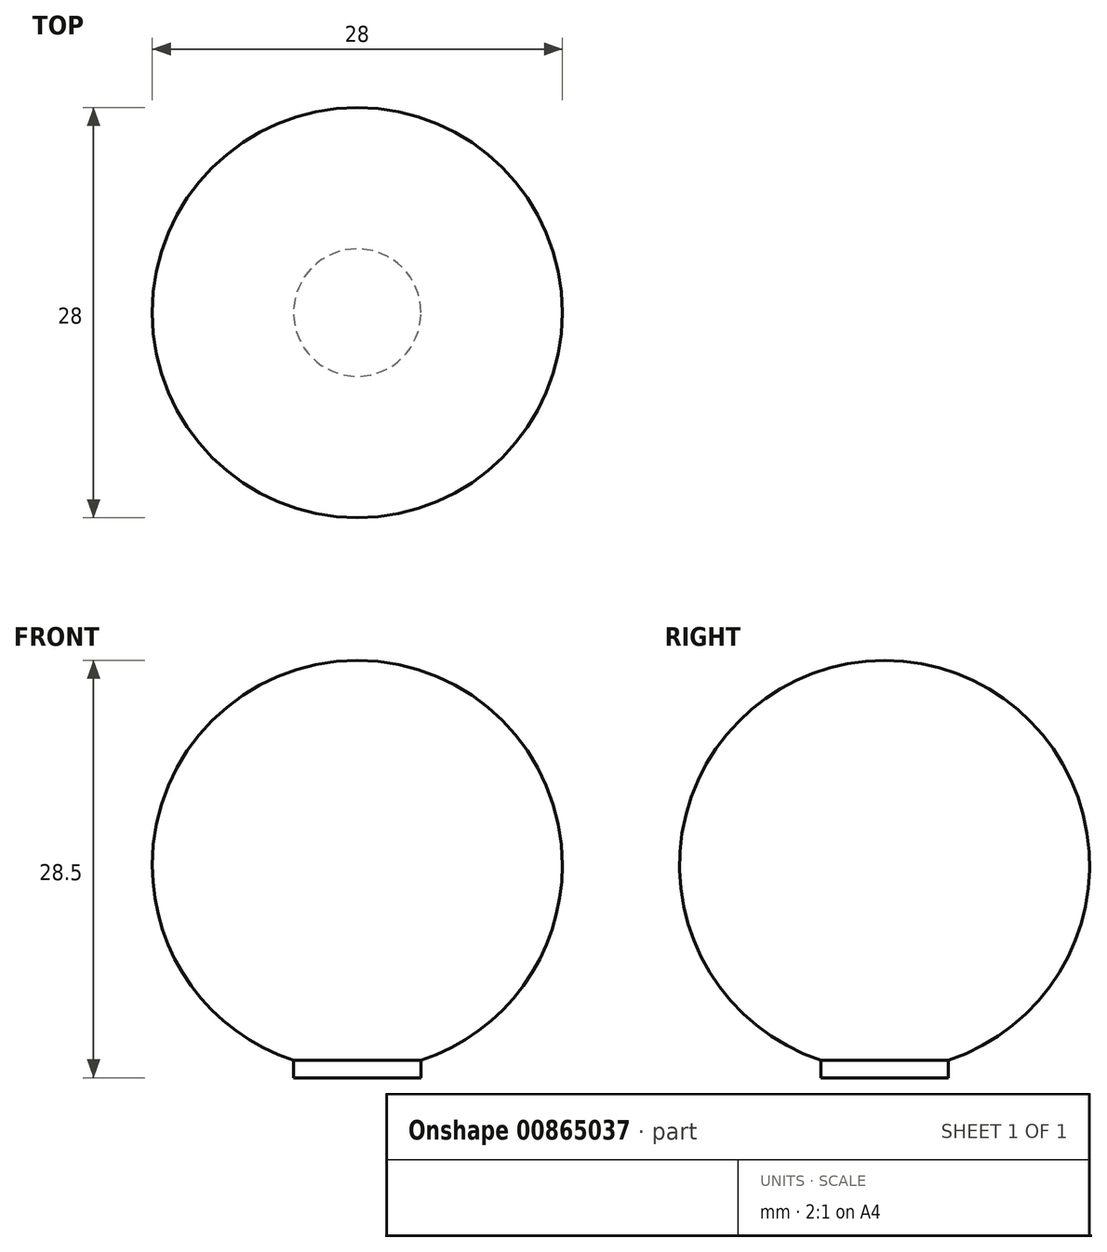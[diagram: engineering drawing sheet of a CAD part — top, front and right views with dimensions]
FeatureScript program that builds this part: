
annotation { "Feature Type Name" : "Feature", "Feature Type Description" : "" }
export const myFeature = defineFeature(function(context is Context, id is Id, definition is map)
    precondition{}
    {
        {
            var Q0;
            Q0=qCreatedBy(makeId("Front.planeOp"),FACE);
            var sketch = newSketch(context, id + "F0", { "sketchPlane" : qUnion([Q0])});
            skCircle(sketch, "E0", {"center": v(0, 0) * mm, "radius": 14 * mm});
            skLineSegment(sketch, "E1", {"start": v(-14, 0) * mm, "end": v(14, 0) * mm});
            skSolve(sketch);
        }
        {
            var Q0;
            {var subQ0=sQuery(id+"F0.wireOp",EDGE,"E1");Q0=makeQuery(id+"F0.imprint","IMPRINT",FACE,{"disambiguationData":[TD([[makeQuery(id+"F0.imprint","IMPRINT",EDGE,{"derivedFrom":subQ0}),-1.0]])]});}
            var Q1;
            Q1=sQuery(id+"F0.wireOp",EDGE,"E1");
            revolve(context, id + "F1", {"surfaceOperationType" : NewSurfaceOperationType.NEW, "entities" : qUnion([Q0]), "axis" : qUnion([Q1]), "revolveType" : RevolveType.FULL});
        }
        {
            var Q0;
            Q0=qCreatedBy(makeId("Top.planeOp"),FACE);
            cPlane(context, id + "F2", {"entities" : qUnion([Q0]), "cplaneType" : CPlaneType.OFFSET, "offset" : 12.5 * mm, "oppositeDirection" : true, "width" : 150 * mm, "height" : 150 * mm});
        }
        {
            var Q0;
            Q0=qCreatedBy(id+"F2.planeOp",FACE);
            var sketch = newSketch(context, id + "F3", { "sketchPlane" : qUnion([Q0])});
            skCircle(sketch, "E2", {"center": v(0, 0) * mm, "radius": 4.35 * mm});
            skSolve(sketch);
        }
        {
            var Q0;
            Q0 = qSketchRegion(id + "F3", true);
            extrude(context, id + "F4", {"entities" : qUnion([Q0]), "operationType" : NewBodyOperationType.ADD, "oppositeDirection" : true, "depth" : 2 * mm, "offsetDistance" : 25 * mm});
        }
    });
